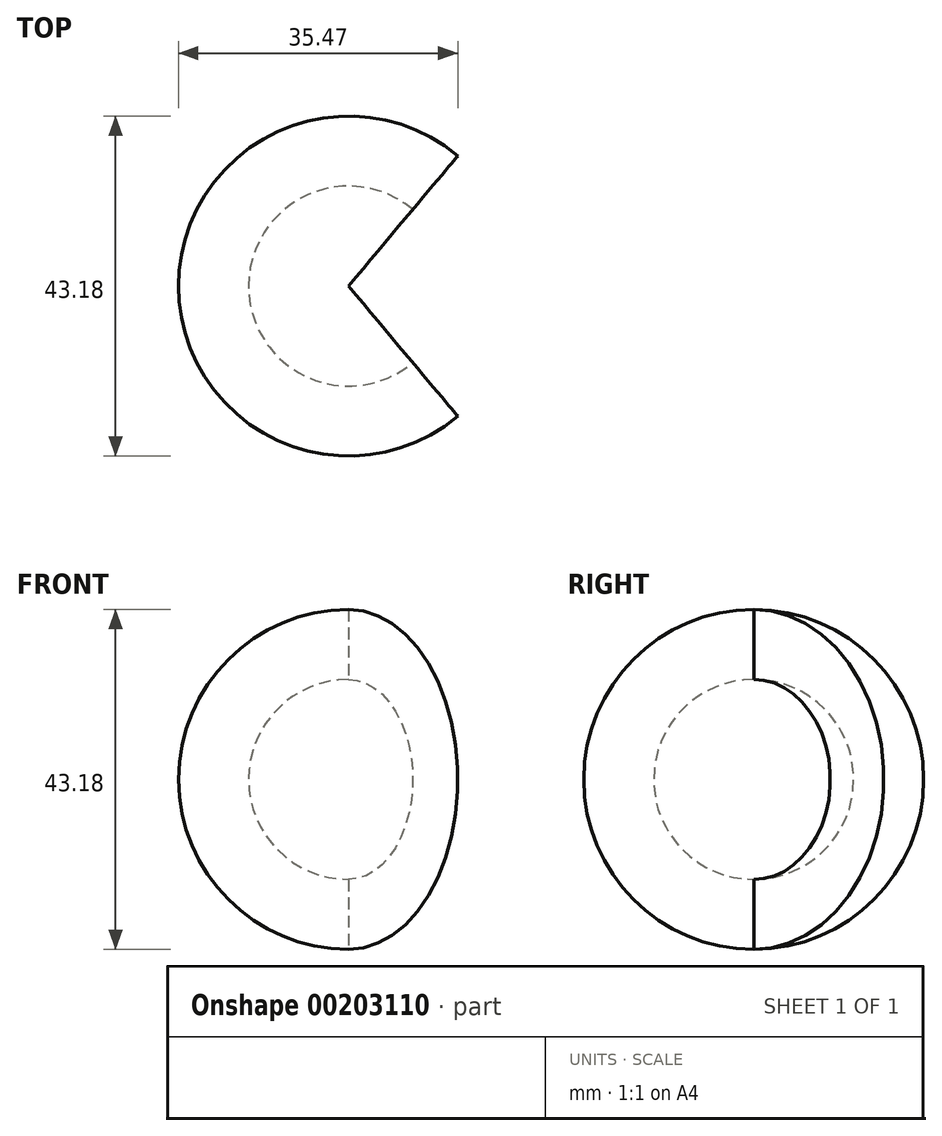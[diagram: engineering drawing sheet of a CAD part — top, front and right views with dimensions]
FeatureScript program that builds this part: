
annotation { "Feature Type Name" : "Feature", "Feature Type Description" : "" }
export const myFeature = defineFeature(function(context is Context, id is Id, definition is map)
    precondition{}
    {
        {
            var Q0;
            Q0=qCreatedBy(makeId("Front.planeOp"),FACE);
            var sketch = newSketch(context, id + "F0", { "sketchPlane" : qUnion([Q0])});
            skArc(sketch, "E0", {"start": v(0, 21.59) * mm, "mid": v(-21.59, 0) * mm, "end": v(0, -21.59) * mm});
            skLineSegment(sketch, "E1", {"start": v(0, 21.59) * mm, "end": v(0, -21.59) * mm});
            skSolve(sketch);
        }
        {
            var Q0;
            Q0 = qSketchRegion(id + "F0", true);
            var Q1;
            Q1=sQuery(id+"F0.wireOp",EDGE,"E1");
            revolve(context, id + "F1", {"entities" : qUnion([Q0]), "axis" : qUnion([Q1]), "revolveType" : RevolveType.SYMMETRIC, "angle" : 260 * degree});
        }
        {
            var Q0;
            Q0=qCreatedBy(makeId("Front.planeOp"),FACE);
            var sketch = newSketch(context, id + "F2", { "sketchPlane" : qUnion([Q0])});
            skArc(sketch, "E2", {"start": v(0, 12.7) * mm, "mid": v(-12.7, 0) * mm, "end": v(0, -12.7) * mm});
            skLineSegment(sketch, "E3", {"start": v(0, 12.7) * mm, "end": v(0, -12.7) * mm});
            skSolve(sketch);
        }
        {
            var Q0;
            Q0 = qSketchRegion(id + "F2", true);
            var Q1;
            Q1=sQuery(id+"F2.wireOp",EDGE,"E3");
            revolve(context, id + "F3", {"operationType" : NewBodyOperationType.REMOVE, "entities" : qUnion([Q0]), "axis" : qUnion([Q1]), "revolveType" : RevolveType.FULL, "oppositeDirection" : true});
        }
    });
